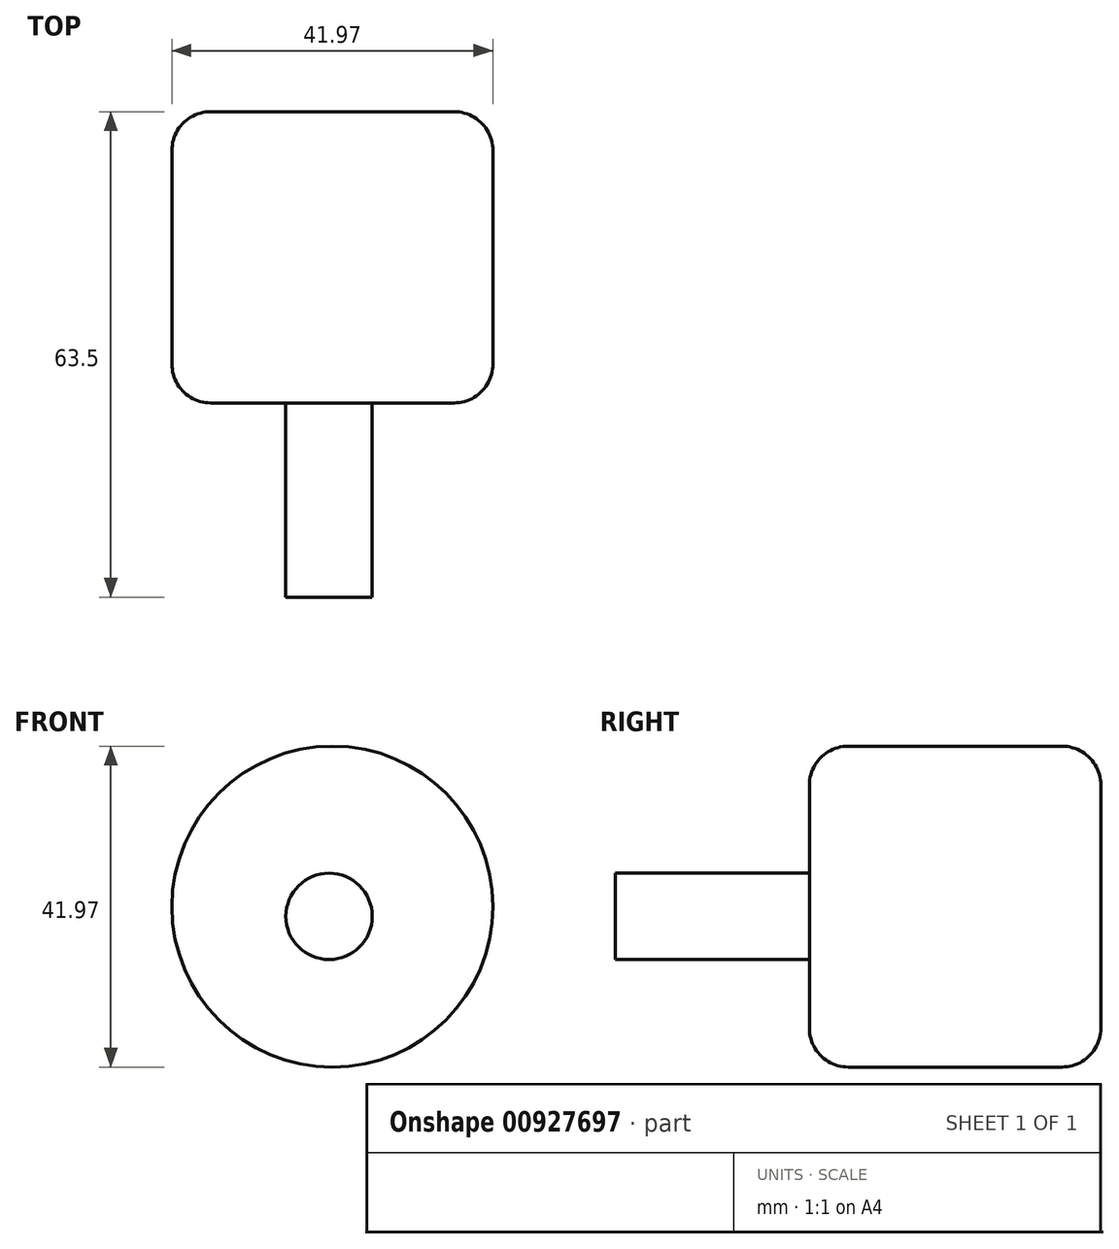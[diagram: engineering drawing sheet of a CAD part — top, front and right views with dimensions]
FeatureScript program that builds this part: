
annotation { "Feature Type Name" : "Feature", "Feature Type Description" : "" }
export const myFeature = defineFeature(function(context is Context, id is Id, definition is map)
    precondition{}
    {
        {
            var Q0;
            Q0=qCreatedBy(makeId("Front.planeOp"),FACE);
            var sketch = newSketch(context, id + "F0", { "sketchPlane" : qUnion([Q0])});
            skCircle(sketch, "E0", {"center": v(-26.21, 26.8) * mm, "radius": 20.99 * mm});
            skSolve(sketch);
        }
        {
            var Q0;
            Q0=makeQuery(id+"F0.imprint","IMPRINT",FACE,{"disambiguationData":[TD([[makeQuery(id+"F0.imprint","IMPRINT",EDGE,{"derivedFrom":sQuery(id+"F0.wireOp",EDGE,"E0")}),1.0]])]});
            extrude(context, id + "F1", {"entities" : qUnion([Q0]), "oppositeDirection" : true, "depth" : 38.1 * mm, "offsetDistance" : 25.4 * mm});
        }
        {
            var Q0;
            Q0=makeQuery(id+"F1.opExtrude","CAP_EDGE",EDGE,{"disambiguationData":[OSD([sQuery(id+"F0.wireOp",EDGE,"E0")])],"isStart":true});
            var Q1;
            Q1=makeQuery(id+"F1.opExtrude","SWEPT_FACE",FACE,{"disambiguationData":[OSD([sQuery(id+"F0.wireOp",EDGE,"E0")])]});
            fillet(context, id + "F2", {"entities" : qUnion([Q0, Q1]), "radius" : 5.08 * mm, "tangentPropagation" : true, "allowEdgeOverflow" : false});
        }
        {
            var Q0;
            Q0=qCreatedBy(makeId("Front.planeOp"),FACE);
            var sketch = newSketch(context, id + "F3", { "sketchPlane" : qUnion([Q0])});
            skCircle(sketch, "E1", {"center": v(-26.64, 25.52) * mm, "radius": 5.65 * mm});
            skSolve(sketch);
        }
        {
            var Q0;
            Q0=makeQuery(id+"F3.imprint","IMPRINT",FACE,{"disambiguationData":[TD([[makeQuery(id+"F3.imprint","IMPRINT",EDGE,{"derivedFrom":sQuery(id+"F3.wireOp",EDGE,"E1")}),1.0]])]});
            extrude(context, id + "F4", {"entities" : qUnion([Q0]), "operationType" : NewBodyOperationType.ADD, "depth" : 25.4 * mm, "offsetDistance" : 25.4 * mm});
        }
    });
